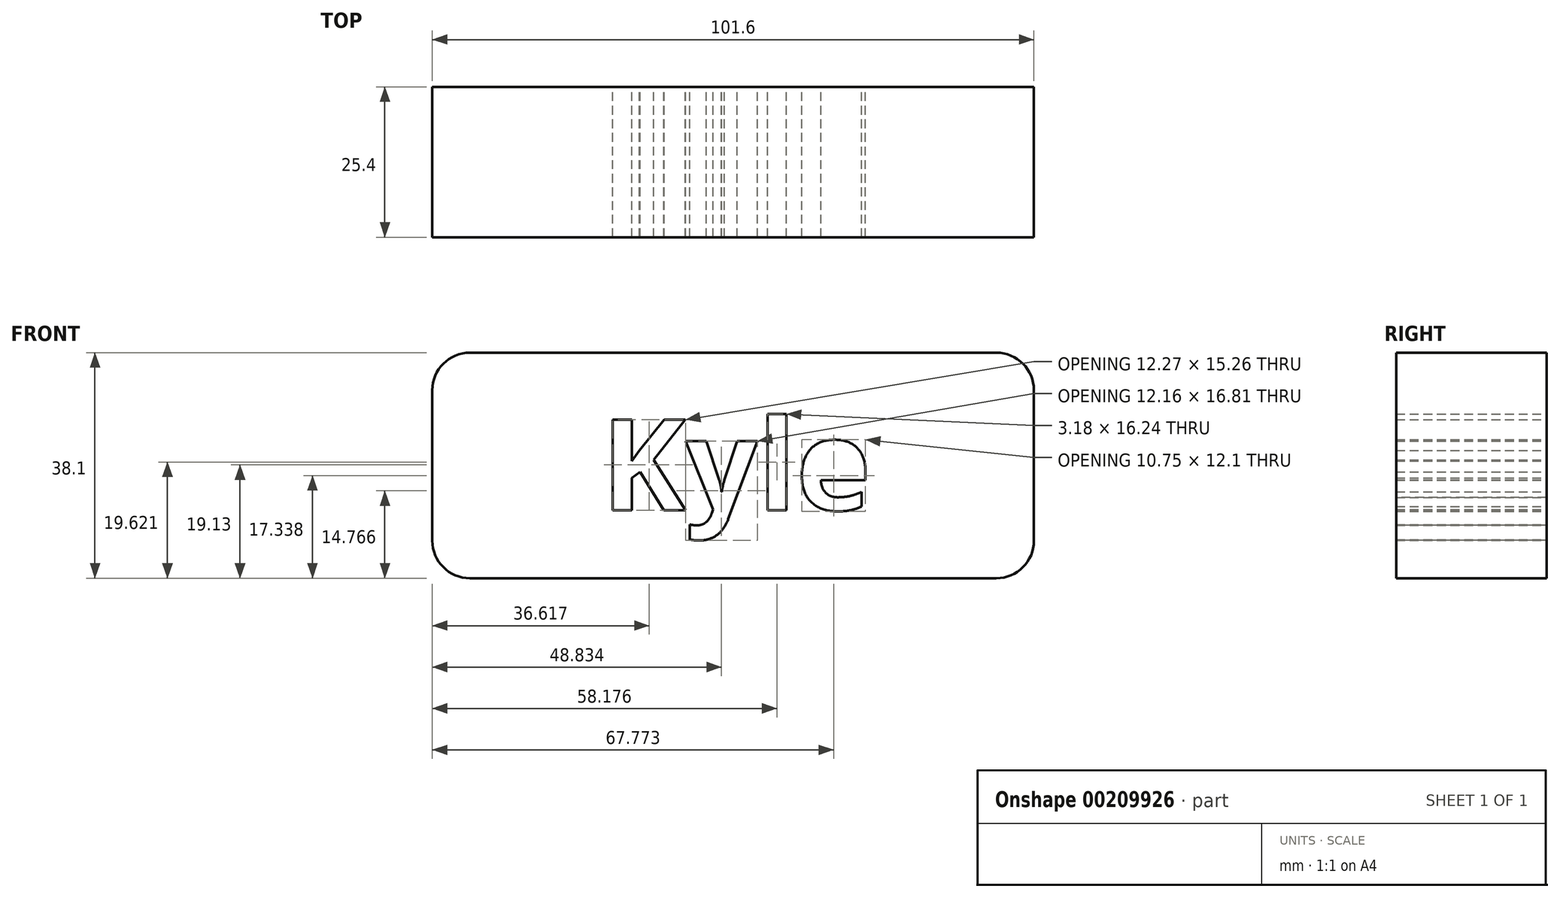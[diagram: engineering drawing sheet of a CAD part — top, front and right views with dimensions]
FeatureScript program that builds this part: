
annotation { "Feature Type Name" : "Feature", "Feature Type Description" : "" }
export const myFeature = defineFeature(function(context is Context, id is Id, definition is map)
    precondition{}
    {
        {
            var Q0;
            Q0=qCreatedBy(makeId("Front.planeOp"),FACE);
            var sketch = newSketch(context, id + "F0", { "sketchPlane" : qUnion([Q0])});
            skLineSegment(sketch, "E0.bottom", {"start": v(44.45, 19.05) * mm, "end": v(-44.45, 19.05) * mm});
            skLineSegment(sketch, "E0.top", {"start": v(44.45, -19.05) * mm, "end": v(-44.45, -19.05) * mm});
            skLineSegment(sketch, "E0.left", {"start": v(50.8, 12.7) * mm, "end": v(50.8, -12.7) * mm});
            skLineSegment(sketch, "E0.right", {"start": v(-50.8, 12.7) * mm, "end": v(-50.8, -12.7) * mm});
            skPoint(sketch, "E0.middle", {"position": v(0, 0) * mm});
            skPoint(sketch, "E1.visualSharp", {"position": v(-50.8, 19.05) * mm});
            skArc(sketch, "E1.filletArc", {"start": v(-44.45, 19.05) * mm, "mid": v(-48.94, 17.2) * mm, "end": v(-50.8, 12.7) * mm});
            skPoint(sketch, "E2.visualSharp", {"position": v(-50.8, -19.05) * mm});
            skArc(sketch, "E2.filletArc", {"start": v(-50.8, -12.7) * mm, "mid": v(-48.94, -17.2) * mm, "end": v(-44.45, -19.05) * mm});
            skPoint(sketch, "E3.visualSharp", {"position": v(50.8, 19.05) * mm});
            skArc(sketch, "E3.filletArc", {"start": v(50.8, 12.7) * mm, "mid": v(48.94, 17.2) * mm, "end": v(44.45, 19.05) * mm});
            skPoint(sketch, "E4.visualSharp", {"position": v(50.8, -19.05) * mm});
            skArc(sketch, "E4.filletArc", {"start": v(44.45, -19.05) * mm, "mid": v(48.94, -17.2) * mm, "end": v(50.8, -12.7) * mm});
            skText(sketch, "E5", { "text": "Kyle", "fontName": "OpenSans-Bold.ttf"});
            const initialGuessF0  = {"E5": [-0.02224, -0.00755, 1, 0, 0.01539]};
            skSetInitialGuess(sketch, initialGuessF0);
            skSolve(sketch);
        }
        {
            var Q0;
            Q0 = qSketchRegion(id + "F0", true);
            extrude(context, id + "F1", {"entities" : qUnion([Q0]), "depth" : 25.4 * mm});
        }
    });
